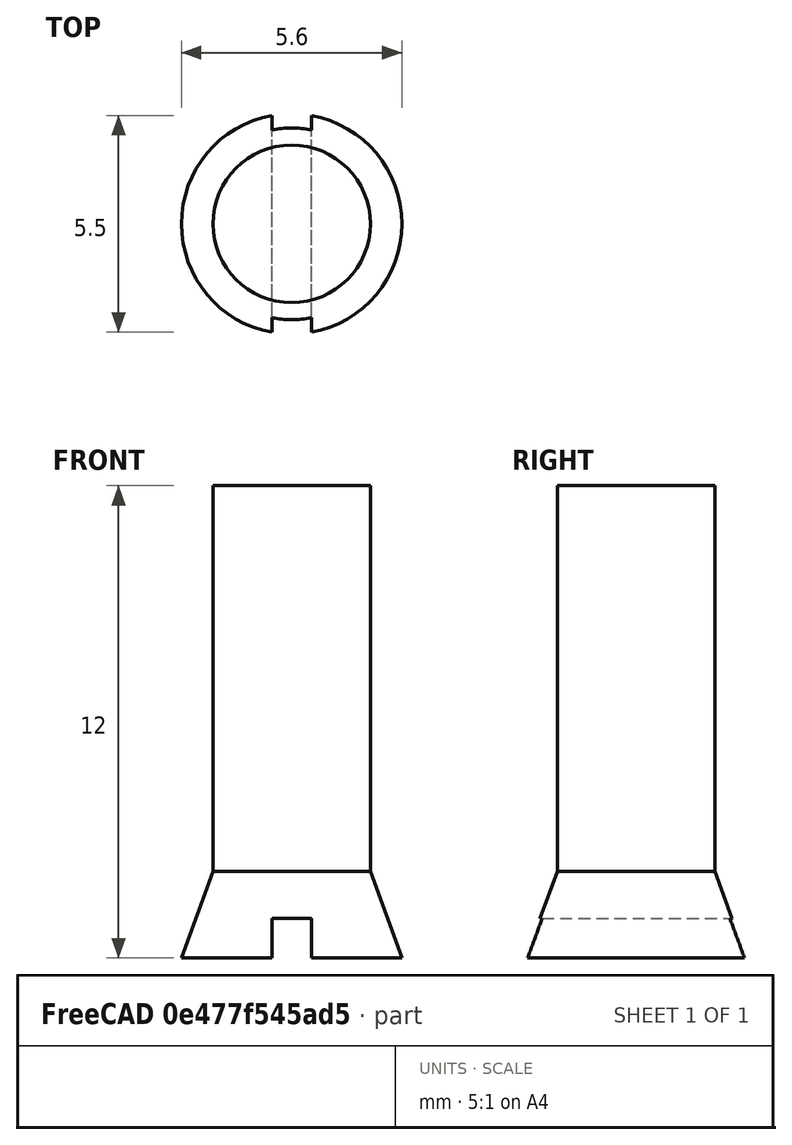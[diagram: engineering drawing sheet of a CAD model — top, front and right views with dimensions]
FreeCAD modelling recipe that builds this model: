
FCSTD DOCUMENT  (FreeCAD 1.0R39319 (Git))
Label: ojt1_t14r01_screw
License: All rights reserved
LicenseURL: https://en.wikipedia.org/wiki/All_rights_reserved
objects: Part::Cylinder×1, Part::Cone×1, Part::Box×1, Part::Cut×1, Part::MultiFuse×1
note: 5 computed .brp shape members not serialized (recipe doc carries the construction recipe); baked Part::Feature solids carry a one-line shape summary decoded from their .brp

FEATURE [Part::Cylinder] Cylinder
  Angle = 360
  AttacherType = Attacher::AttachEngine3D
  FirstAngle = 0
  Height = 10
  Placement = pos=(0,0,2) rot=(0,0,1;0rad)
  Radius = 2
  SecondAngle = 0
FEATURE [Part::Cone] Cone
  Angle = 360
  AttacherType = Attacher::AttachEngine3D
  Height = 2.2
  Radius1 = 2.8
  Radius2 = 2
FEATURE [Part::Box] Box  label="Cube"
  AttacherType = Attacher::AttachEngine3D
  Height = 1
  Length = 1
  Placement = pos=(-0.5,-5,0) rot=(0,0,1;0rad)
  Width = 10
FEATURE [Part::Cut] Cut
  Base = -> Cone
  Refine = true
  Tool = -> Box
FEATURE [Part::MultiFuse] Fusion
  Refine = true
  Shapes = -> [Cylinder,Cut]
